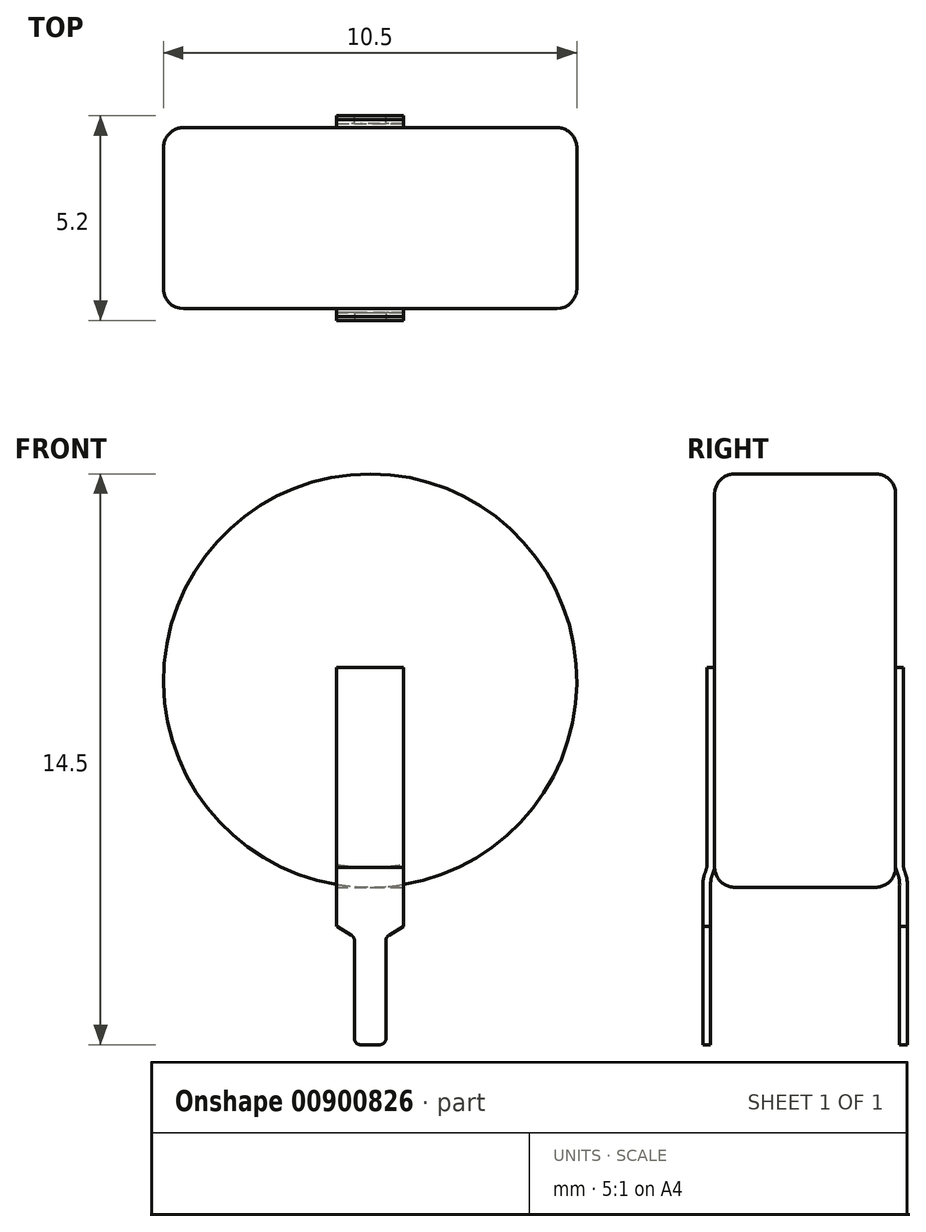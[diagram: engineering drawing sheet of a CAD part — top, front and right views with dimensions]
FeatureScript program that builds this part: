
annotation { "Feature Type Name" : "Feature", "Feature Type Description" : "" }
export const myFeature = defineFeature(function(context is Context, id is Id, definition is map)
    precondition{}
    {
        {
            var Q0;
            Q0=qCreatedBy(makeId("Front.planeOp"),FACE);
            var sketch = newSketch(context, id + "F0", { "sketchPlane" : qUnion([Q0])});
            skCircle(sketch, "E0", {"center": v(0, 0) * mm, "radius": 5.25 * mm});
            skSolve(sketch);
        }
        {
            var Q0;
            Q0=makeQuery(id+"F0.imprint","IMPRINT",FACE,{"disambiguationData":[TD([[makeQuery(id+"F0.imprint","IMPRINT",EDGE,{"derivedFrom":sQuery(id+"F0.wireOp",EDGE,"E0")}),1.0]])]});
            extrude(context, id + "F1", {"entities" : qUnion([Q0]), "depth" : 4.6 * mm, "offsetDistance" : 25.4 * mm});
        }
        {
            var Q0;
            Q0=makeQuery(id+"F1.opExtrude","CAP_EDGE",EDGE,{"disambiguationData":[OSD([sQuery(id+"F0.wireOp",EDGE,"E0")])],"isStart":false});
            var Q1;
            Q1=makeQuery(id+"F1.opExtrude","CAP_EDGE",EDGE,{"disambiguationData":[OSD([sQuery(id+"F0.wireOp",EDGE,"E0")])],"isStart":true});
            fillet(context, id + "F2", {"entities" : qUnion([Q0, Q1]), "radius" : 0.5 * mm, "tangentPropagation" : true, "allowEdgeOverflow" : false});
        }
        {
            var Q0;
            Q0=makeQuery(id+"F1.opExtrude","CAP_FACE",FACE,{"disambiguationData":[OSD([sQuery(id+"F0.wireOp",EDGE,"E0")])],"isStart":true});
            var sketch = newSketch(context, id + "F3", { "sketchPlane" : qUnion([Q0])});
            skLineSegment(sketch, "E1.bottom", {"start": v(-0.84, 0.34) * mm, "end": v(0.86, 0.34) * mm});
            skLineSegment(sketch, "E1.top", {"start": v(-0.84, -4.74) * mm, "end": v(0.86, -4.74) * mm});
            skLineSegment(sketch, "E1.left", {"start": v(-0.84, 0.34) * mm, "end": v(-0.84, -4.74) * mm});
            skLineSegment(sketch, "E1.right", {"start": v(0.86, 0.34) * mm, "end": v(0.86, -4.74) * mm});
            skSolve(sketch);
        }
        {
            var Q0;
            {var subQ5=sQuery(id+"F3.wireOp",EDGE,"E1.bottom");Q0=makeQuery(id+"F3.imprint","IMPRINT",FACE,{"disambiguationData":[TD([[makeQuery(id+"F3.imprint","IMPRINT",EDGE,{"derivedFrom":subQ5}),-1.0]])]});}
            var Q1;
            {var subQ0=sQuery(id+"F3.wireOp",EDGE,"E1.left");var subQ1=sQuery(id+"F3.wireOp",EDGE,"E1.top");var subQ2=makeQuery(id+"F3.imprint","INTERSECT",VERTEX,{"derivedFrom":[subQ1,subQ0]});Q1=makeQuery(id+"F3.imprint","IMPRINT",FACE,{"disambiguationData":[TD([[makeQuery(id+"F3.imprint","IMPRINT",EDGE,{"disambiguationData":[TD([[subQ2,-1.0]])],"derivedFrom":subQ1}),1.0]])]});}
            var Q2;
            {var subQ0=sQuery(id+"F3.wireOp",EDGE,"E1.right");var subQ1=sQuery(id+"F3.wireOp",EDGE,"E1.top");var subQ2=makeQuery(id+"F3.imprint","INTERSECT",VERTEX,{"derivedFrom":[subQ1,subQ0]});Q2=makeQuery(id+"F3.imprint","IMPRINT",FACE,{"disambiguationData":[TD([[makeQuery(id+"F3.imprint","IMPRINT",EDGE,{"disambiguationData":[TD([[subQ2,1.0]])],"derivedFrom":subQ1}),1.0]])]});}
            extrude(context, id + "F4", {"entities" : qUnion([Q0, Q1, Q2]), "operationType" : NewBodyOperationType.ADD, "depth" : .2 * mm, "offsetDistance" : 25.4 * mm});
        }
        {
            var Q0;
            Q0=makeQuery(id+"F1.opExtrude","CAP_FACE",FACE,{"disambiguationData":[OSD([sQuery(id+"F0.wireOp",EDGE,"E0")])],"isStart":false});
            var sketch = newSketch(context, id + "F5", { "sketchPlane" : qUnion([Q0])});
            skLineSegment(sketch, "E2.0", {"start": v(0.84, 0.34) * mm, "end": v(0.84, -4.74) * mm});
            skLineSegment(sketch, "E3.0", {"start": v(0.84, 0.34) * mm, "end": v(-0.86, 0.34) * mm});
            skLineSegment(sketch, "E4.0", {"start": v(-0.86, 0.34) * mm, "end": v(-0.86, -4.74) * mm});
            skLineSegment(sketch, "E5.0", {"start": v(0.84, -4.74) * mm, "end": v(-0.86, -4.74) * mm});
            skSolve(sketch);
        }
        {
            var Q0;
            {var subQ0=sQuery(id+"F5.wireOp",EDGE,"E5.0");var subQ1=sQuery(id+"F5.wireOp",EDGE,"E4.0");var subQ2=makeQuery(id+"F5.imprint","INTERSECT",VERTEX,{"derivedFrom":[subQ1,subQ0]});Q0=makeQuery(id+"F5.imprint","IMPRINT",FACE,{"disambiguationData":[TD([[makeQuery(id+"F5.imprint","IMPRINT",EDGE,{"disambiguationData":[TD([[subQ2,1.0]])],"derivedFrom":subQ1}),1.0]])]});}
            var Q1;
            {var subQ6=sQuery(id+"F5.wireOp",EDGE,"E3.0");Q1=makeQuery(id+"F5.imprint","IMPRINT",FACE,{"disambiguationData":[TD([[makeQuery(id+"F5.imprint","IMPRINT",EDGE,{"derivedFrom":subQ6}),1.0]])]});}
            var Q2;
            {var subQ0=sQuery(id+"F5.wireOp",EDGE,"E5.0");var subQ1=sQuery(id+"F5.wireOp",EDGE,"E2.0");var subQ2=makeQuery(id+"F5.imprint","INTERSECT",VERTEX,{"derivedFrom":[subQ1,subQ0]});Q2=makeQuery(id+"F5.imprint","IMPRINT",FACE,{"disambiguationData":[TD([[makeQuery(id+"F5.imprint","IMPRINT",EDGE,{"disambiguationData":[TD([[subQ2,1.0]])],"derivedFrom":subQ1}),-1.0]])]});}
            extrude(context, id + "F6", {"entities" : qUnion([Q0, Q1, Q2]), "operationType" : NewBodyOperationType.ADD, "depth" : .2 * mm, "offsetDistance" : 25.4 * mm});
        }
        {
            var Q0;
            Q0=makeQuery(id+"F6.opExtrude","SWEPT_FACE",FACE,{"disambiguationData":[OSD([sQuery(id+"F5.wireOp",EDGE,"E2.0")])]});
            var sketch = newSketch(context, id + "F7", { "sketchPlane" : qUnion([Q0])});
            skLineSegment(sketch, "E6.bottom", {"start": v(-4.9, -5.25) * mm, "end": v(-4.7, -5.25) * mm});
            skLineSegment(sketch, "E6.top", {"start": v(-4.9, -6.25) * mm, "end": v(-4.7, -6.25) * mm});
            skLineSegment(sketch, "E6.left", {"start": v(-4.9, -5.25) * mm, "end": v(-4.9, -6.25) * mm});
            skLineSegment(sketch, "E6.right", {"start": v(-4.7, -5.25) * mm, "end": v(-4.7, -6.25) * mm});
            skLineSegment(sketch, "E7.bottom", {"start": v(0.1, -5.25) * mm, "end": v(0.3, -5.25) * mm});
            skLineSegment(sketch, "E7.top", {"start": v(0.1, -6.25) * mm, "end": v(0.3, -6.25) * mm});
            skLineSegment(sketch, "E7.left", {"start": v(0.1, -5.25) * mm, "end": v(0.1, -6.25) * mm});
            skLineSegment(sketch, "E7.right", {"start": v(0.3, -5.25) * mm, "end": v(0.3, -6.25) * mm});
            skLineSegment(sketch, "E8", {"start": v(-4.1, 5.25) * mm, "end": v(-0.5, 5.25) * mm, "construction": true});
            skLineSegment(sketch, "E9", {"start": v(-0.5, -5.25) * mm, "end": v(-4.1, -5.25) * mm, "construction": true});
            skLineSegment(sketch, "E10", {"start": v(-2.3, -5.25) * mm, "end": v(-2.3, -6.34) * mm, "construction": true});
            skFitSpline(sketch, "E11", {"points": [v(-4.8, -4.74) * mm, v(-4.9, -5.25) * mm], "startDerivative": vector(-0.1, -0.5) * mm, "endDerivative": vector(0, -0.94) * mm});
            skFitSpline(sketch, "E12", {"points": [v(-4.6, -4.74) * mm, v(-4.7, -5.25) * mm], "startDerivative": vector(-0.1, -0.5) * mm, "endDerivative": vector(0.05, -0.8) * mm});
            skFitSpline(sketch, "E13.MirrorCS", {"points": [v(0.2, -4.74) * mm, v(0.3, -5.25) * mm], "startDerivative": vector(0.1, -0.5) * mm, "endDerivative": vector(0, -0.94) * mm});
            skFitSpline(sketch, "E14.MirrorCS", {"points": [v(0, -4.74) * mm, v(0.1, -5.25) * mm], "startDerivative": vector(0.1, -0.5) * mm, "endDerivative": vector(-0.05, -0.8) * mm});
            skLineSegment(sketch, "E15", {"start": v(0, -4.74) * mm, "end": v(0.2, -4.74) * mm});
            skSolve(sketch);
        }
        {
            var Q0;
            Q0=makeQuery(id+"F7.imprint","IMPRINT",FACE,{"disambiguationData":[TD([[makeQuery(id+"F7.imprint","IMPRINT",EDGE,{"derivedFrom":sQuery(id+"F7.wireOp",EDGE,"E6.bottom")}),-1.0]])]});
            var Q1;
            Q1=makeQuery(id+"F7.imprint","IMPRINT",FACE,{"disambiguationData":[TD([[makeQuery(id+"F7.imprint","IMPRINT",EDGE,{"derivedFrom":sQuery(id+"F7.wireOp",EDGE,"E6.bottom")}),1.0]])]});
            var Q2;
            Q2=makeQuery(id+"F7.imprint","IMPRINT",FACE,{"disambiguationData":[TD([[makeQuery(id+"F7.imprint","IMPRINT",EDGE,{"derivedFrom":sQuery(id+"F7.wireOp",EDGE,"E7.top")}),1.0]])]});
            var Q3;
            Q3=makeQuery(id+"F7.imprint","IMPRINT",FACE,{"disambiguationData":[TD([[makeQuery(id+"F7.imprint","IMPRINT",EDGE,{"derivedFrom":sQuery(id+"F7.wireOp",EDGE,"E13.MirrorCS")}),-1.0]])]});
            var Q4;
            Q4=makeQuery(id+"F6.opExtrude","SWEPT_FACE",FACE,{"disambiguationData":[OSD([sQuery(id+"F5.wireOp",EDGE,"E4.0")])]});
            extrude(context, id + "F8", {"entities" : qUnion([Q0, Q1, Q2, Q3]), "operationType" : NewBodyOperationType.ADD, "endBound" : BoundingType.UP_TO_SURFACE, "oppositeDirection" : true, "depth" : 25.4 * mm, "endBoundEntityFace" : qUnion([Q4]), "offsetDistance" : 25.4 * mm});
        }
        {
            var Q0;
            Q0=makeQuery(id+"F8.opExtrude","SWEPT_FACE",FACE,{"disambiguationData":[OSD([sQuery(id+"F7.wireOp",EDGE,"E7.right")])]});
            var sketch = newSketch(context, id + "F9", { "sketchPlane" : qUnion([Q0])});
            skLineSegment(sketch, "E16.bottom", {"start": v(-0.4, -6.25) * mm, "end": v(0.4, -6.25) * mm});
            skLineSegment(sketch, "E16.top", {"start": v(-0.25, -9.25) * mm, "end": v(0.25, -9.25) * mm});
            skLineSegment(sketch, "E16.left", {"start": v(-0.4, -6.6) * mm, "end": v(-0.4, -9.1) * mm});
            skLineSegment(sketch, "E16.right", {"start": v(0.4, -6.6) * mm, "end": v(0.4, -9.1) * mm});
            skLineSegment(sketch, "E17", {"start": v(-0.84, -6.25) * mm, "end": v(-0.47, -6.47) * mm});
            skLineSegment(sketch, "E18.MirrorCS", {"start": v(0.84, -6.25) * mm, "end": v(0.47, -6.47) * mm});
            skPoint(sketch, "E19.visualSharp", {"position": v(-0.4, -9.25) * mm});
            skArc(sketch, "E19.filletArc", {"start": v(-0.4, -9.1) * mm, "mid": v(-0.36, -9.2) * mm, "end": v(-0.25, -9.25) * mm});
            skPoint(sketch, "E20.visualSharp", {"position": v(0.4, -9.25) * mm});
            skArc(sketch, "E20.filletArc", {"start": v(0.25, -9.25) * mm, "mid": v(0.36, -9.2) * mm, "end": v(0.4, -9.1) * mm});
            skPoint(sketch, "E21.newPointA", {"position": v(-0.4, -6.52) * mm});
            skArc(sketch, "E21.filletArc", {"start": v(-0.4, -6.6) * mm, "mid": v(-0.42, -6.53) * mm, "end": v(-0.47, -6.47) * mm});
            skPoint(sketch, "E22.newPointA", {"position": v(0.4, -6.25) * mm});
            skPoint(sketch, "E22.newPointB", {"position": v(0.4, -6.52) * mm});
            skArc(sketch, "E22.filletArc", {"start": v(0.47, -6.47) * mm, "mid": v(0.42, -6.53) * mm, "end": v(0.4, -6.6) * mm});
            skSolve(sketch);
        }
        {
            var Q0;
            {var subQ2=sQuery(id+"F9.wireOp",EDGE,"E16.bottom");Q0=makeQuery(id+"F9.imprint","IMPRINT",FACE,{"disambiguationData":[TD([[makeQuery(id+"F9.imprint","IMPRINT",EDGE,{"derivedFrom":subQ2}),1.0]])]});}
            var Q1;
            Q1=makeQuery(id+"F8.opExtrude","SWEPT_FACE",FACE,{"disambiguationData":[OSD([sQuery(id+"F7.wireOp",EDGE,"E7.left")])]});
            extrude(context, id + "F10", {"entities" : qUnion([Q0]), "operationType" : NewBodyOperationType.ADD, "endBound" : BoundingType.UP_TO_SURFACE, "oppositeDirection" : true, "depth" : 25.4 * mm, "endBoundEntityFace" : qUnion([Q1]), "offsetDistance" : 25.4 * mm});
        }
        {
            var Q0;
            Q0=makeQuery(id+"F8.opExtrude","SWEPT_FACE",FACE,{"disambiguationData":[OSD([sQuery(id+"F7.wireOp",EDGE,"E6.left")])]});
            var sketch = newSketch(context, id + "F11", { "sketchPlane" : qUnion([Q0])});
            skPoint(sketch, "E23.0", {"position": v(-0.84, -6.25) * mm});
            skLineSegment(sketch, "E24.0", {"start": v(-0.4, -6.6) * mm, "end": v(-0.4, -9.1) * mm});
            skLineSegment(sketch, "E25.0", {"start": v(0.4, -6.6) * mm, "end": v(0.4, -9.1) * mm});
            skArc(sketch, "E26.0", {"start": v(0.4, -6.6) * mm, "mid": v(0.42, -6.53) * mm, "end": v(0.47, -6.47) * mm});
            skLineSegment(sketch, "E27.0", {"start": v(0.84, -6.25) * mm, "end": v(0.47, -6.47) * mm});
            skLineSegment(sketch, "E28.0", {"start": v(-0.84, -6.25) * mm, "end": v(-0.47, -6.47) * mm});
            skArc(sketch, "E29.0", {"start": v(-0.47, -6.47) * mm, "mid": v(-0.42, -6.53) * mm, "end": v(-0.4, -6.6) * mm});
            skLineSegment(sketch, "E30.0", {"start": v(0.25, -9.25) * mm, "end": v(-0.25, -9.25) * mm});
            skArc(sketch, "E31.0", {"start": v(0.4, -9.1) * mm, "mid": v(0.36, -9.2) * mm, "end": v(0.25, -9.25) * mm});
            skArc(sketch, "E32.0", {"start": v(-0.25, -9.25) * mm, "mid": v(-0.36, -9.2) * mm, "end": v(-0.4, -9.1) * mm});
            skSolve(sketch);
        }
        {
            var Q0;
            Q0 = qSketchRegion(id + "F11", true);
            var Q1;
            Q1=makeQuery(id+"F11.imprint","IMPRINT",FACE,{"disambiguationData":[TD([[makeQuery(id+"F11.imprint","IMPRINT",EDGE,{"derivedFrom":sQuery(id+"F11.wireOp",EDGE,"E24.0")}),1.0]])]});
            var Q2;
            Q2=makeQuery(id+"F8.opExtrude","SWEPT_FACE",FACE,{"disambiguationData":[OSD([sQuery(id+"F7.wireOp",EDGE,"E6.right")])]});
            extrude(context, id + "F12", {"entities" : qUnion([Q0, Q1]), "operationType" : NewBodyOperationType.ADD, "endBound" : BoundingType.UP_TO_SURFACE, "oppositeDirection" : true, "depth" : 25.4 * mm, "endBoundEntityFace" : qUnion([Q2]), "offsetDistance" : 25.4 * mm});
        }
    });
